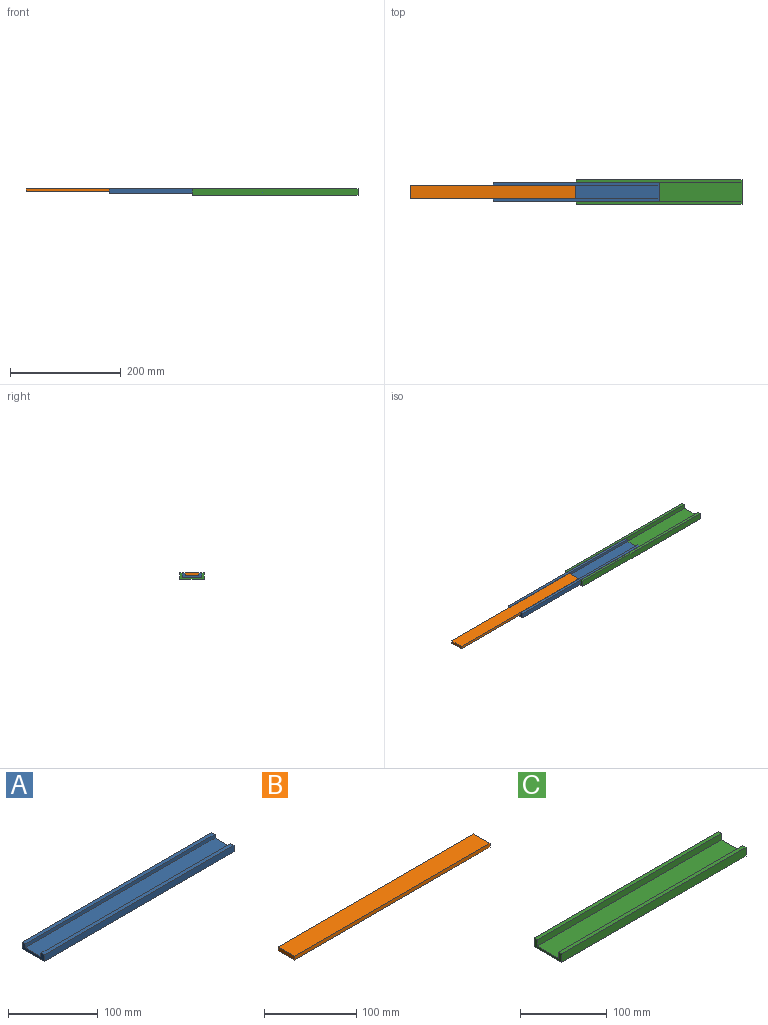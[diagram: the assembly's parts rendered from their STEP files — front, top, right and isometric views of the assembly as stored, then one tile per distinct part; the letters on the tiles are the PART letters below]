
ASSEMBLY  parts=3 mates=2
PART A: 10 faces, bbox 300x35x9 mm
  f0: plane 300x5mm, normal (0,0,1), area 1500mm2, adj f1,f2,f4,f7
  f1: plane 35x9mm, normal (-1,0,0), area 190mm2, adj f0,f2,f3,f5,f6,f7,f8,f9
  f2: plane 300x9mm, normal (0,1,0), area 2700mm2, adj f0,f1,f4,f5
  f3: plane 300x9mm, normal (0,-1,0), area 2700mm2, adj f1,f4,f5,f6
  f4: plane 35x9mm, normal (1,0,0), area 190mm2, adj f0,f2,f3,f5,f6,f7,f8,f9
  f5: plane 300x35mm, normal (0,0,-1), area 10500mm2, adj f1,f2,f3,f4
  f6: plane 300x5mm, normal (0,0,1), area 1500mm2, adj f1,f3,f4,f8
  f7: plane 300x5mm, normal (0,-1,0), area 1500mm2, adj f0,f1,f4,f9
  f8: plane 300x5mm, normal (0,1,0), area 1500mm2, adj f1,f4,f6,f9
  f9: plane 300x25mm, normal (0,0,1), area 7500mm2, adj f1,f4,f7,f8
PART B: 6 faces, bbox 300x25x5 mm
  f0: plane 300x5mm, normal (0,1,0), area 1500mm2, adj f1,f3,f4,f5
  f1: plane 25x5mm, normal (-1,0,0), area 125mm2, adj f0,f2,f4,f5
  f2: plane 300x5mm, normal (0,-1,0), area 1500mm2, adj f1,f3,f4,f5
  f3: plane 25x5mm, normal (1,0,0), area 125mm2, adj f0,f2,f4,f5
  f4: plane 300x25mm, normal (0,0,-1), area 7500mm2, adj f0,f1,f2,f3
  f5: plane 300x25mm, normal (0,0,1), area 7500mm2, adj f0,f1,f2,f3
PART C: 10 faces, bbox 300x45x12 mm
  f0: plane 300x5mm, normal (0,0,1), area 1500mm2, adj f1,f2,f3,f7
  f1: plane 45x12mm, normal (1,0,0), area 225mm2, adj f0,f2,f4,f5,f6,f7,f8,f9
  f2: plane 300x12mm, normal (0,1,0), area 3600mm2, adj f0,f1,f3,f6
  f3: plane 45x12mm, normal (-1,0,0), area 225mm2, adj f0,f2,f4,f5,f6,f7,f8,f9
  f4: plane 300x12mm, normal (0,-1,0), area 3600mm2, adj f1,f3,f5,f6
  f5: plane 300x5mm, normal (0,0,1), area 1500mm2, adj f1,f3,f4,f8
  f6: plane 300x45mm, normal (0,0,-1), area 13500mm2, adj f1,f2,f3,f4
  f7: plane 300x9mm, normal (0,-1,0), area 2700mm2, adj f0,f1,f3,f9
  f8: plane 300x9mm, normal (0,1,0), area 2700mm2, adj f1,f3,f5,f9
  f9: plane 300x35mm, normal (0,0,1), area 10500mm2, adj f1,f3,f7,f8
PLACE A t=(-150,0,-10.6)mm
PLACE B t=(-300,0,-10.6)mm
PLACE C t=(0,0,-10.6)mm fixed
MATE slider B.f3 <-> A.f4  axis (1,0,0) through (-124.42,-15.56,-3.6)mm
MATE slider C.f1 <-> A.f4  axis (1,0,0) through (175.58,-20.56,-7.6)mm
